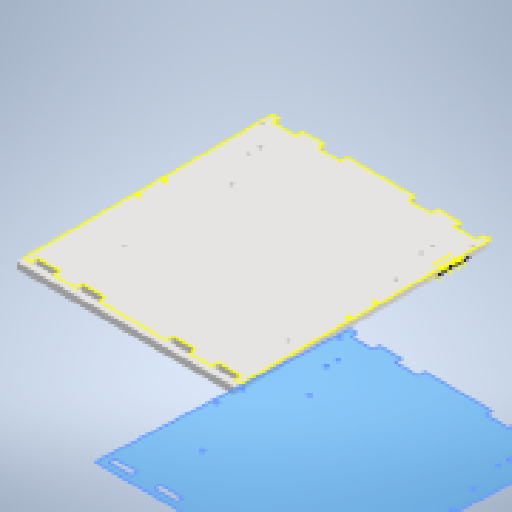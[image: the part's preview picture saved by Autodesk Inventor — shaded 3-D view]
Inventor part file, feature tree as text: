
AUTODESK INVENTOR PART (.ipt)
format: ipt  version: 2024.2 (Build 282272000, 272)  size: 425,472 bytes
history: native  units: mm
features: reference x103, other x9, sketch x8, extrude x7, mirror x2, projected_geometry x1
ambient origin geometry x8: Origin, YZ Plane, XZ Plane, XY Plane, X Axis, Y Axis, Z Axis, Center Point
bodies: Body1 (feature_tree)
feature tree (130):
  extrude  "Выдавливание2"  Depth=192.0mm
  extrude  "Выдавливание3"  Depth=170.0mm
  other  "РабПлоскость1"
  mirror  "Зеркальное отражение1"
  extrude  "Выдавливание4"  Depth=220.0mm
  sketch  "Эскиз4"
  extrude  "Выдавливание5"  Depth=11.0mm
  other  "РабПлоскость2"
  mirror  "Зеркальное отражение2"
  extrude  "Выдавливание6"  Depth=3.0mm
  extrude  "Выдавливание7"  Depth=3.0mm
  extrude  "Выдавливание8"  Depth=3.0mm
  sketch  "Эскиз1"
  sketch  "Эскиз2"
  sketch  "Эскиз3"
  reference  "Ссылка1"
  reference  "Ссылка2"
  reference  "Ссылка3"
  reference  "Ссылка4"
  projected_geometry  "Спроецированная петля1"
  reference  "Ссылка5"
  reference  "Ссылка6"
  reference  "Ссылка7"
  reference  "Ссылка8"
  reference  "Ссылка9"
  reference  "Ссылка10"
  reference  "Ссылка11"
  reference  "Ссылка12"
  reference  "Ссылка13"
  reference  "Ссылка14"
  reference  "Ссылка15"
  reference  "Ссылка16"
  reference  "Ссылка17"
  reference  "Ссылка18"
  reference  "Ссылка19"
  reference  "Ссылка20"
  reference  "Ссылка21"
  reference  "Ссылка22"
  reference  "Ссылка23"
  reference  "Ссылка24"
  reference  "Ссылка25"
  reference  "Ссылка26"
  reference  "Ссылка27"
  reference  "Ссылка28"
  reference  "Ссылка29"
  reference  "Ссылка30"
  reference  "Ссылка31"
  reference  "Ссылка32"
  reference  "Ссылка33"
  reference  "Ссылка34"
  reference  "Ссылка35"
  reference  "Ссылка36"
  reference  "Ссылка37"
  reference  "Ссылка38"
  reference  "Ссылка39"
  reference  "Ссылка40"
  reference  "Ссылка41"
  reference  "Ссылка42"
  reference  "Ссылка43"
  reference  "Ссылка44"
  reference  "Ссылка45"
  reference  "Ссылка46"
  reference  "Ссылка47"
  reference  "Ссылка48"
  reference  "Ссылка49"
  reference  "Ссылка50"
  reference  "Ссылка51"
  reference  "Ссылка52"
  reference  "Ссылка53"
  reference  "Ссылка54"
  reference  "Ссылка55"
  reference  "Ссылка56"
  reference  "Ссылка57"
  reference  "Ссылка58"
  reference  "Ссылка59"
  reference  "Ссылка60"
  reference  "Ссылка61"
  reference  "Ссылка62"
  reference  "Ссылка63"
  reference  "Ссылка64"
  reference  "Ссылка65"
  reference  "Ссылка66"
  reference  "Ссылка67"
  reference  "Ссылка68"
  reference  "Ссылка69"
  reference  "Ссылка70"
  reference  "Ссылка71"
  reference  "Ссылка72"
  reference  "Ссылка73"
  reference  "Ссылка74"
  reference  "Ссылка75"
  reference  "Ссылка76"
  reference  "Ссылка77"
  reference  "Ссылка78"
  reference  "Ссылка79"
  reference  "Ссылка80"
  reference  "Ссылка81"
  reference  "Ссылка82"
  reference  "Ссылка83"
  reference  "Ссылка84"
  reference  "Ссылка85"
  reference  "Ссылка86"
  reference  "Ссылка87"
  reference  "Ссылка88"
  reference  "Ссылка89"
  reference  "Ссылка90"
  reference  "Ссылка91"
  reference  "Ссылка92"
  reference  "Ссылка93"
  reference  "Ссылка94"
  reference  "Ссылка95"
  reference  "Ссылка96"
  reference  "Ссылка97"
  reference  "Ссылка98"
  reference  "Ссылка99"
  reference  "Ссылка100"
  reference  "Ссылка101"
  reference  "Ссылка102"
  reference  "Ссылка103"
  sketch  "Эскиз5"
  sketch  "Эскиз6"
  sketch  "Эскиз7"
  sketch  "Эскиз8"
  other  "<userpath>\Documents\Artist\3D\Робот.iam"
  other  "Робот.iam"
  other  "крепление подшипника_1:1"
  other  "боковая стенка:1"
  other  "Проецирование ребер1"
  other  "Проецирование ребер2"
  other  "Проецирование ребер3"
